# Revit family: BAS-IP_Видеодомофон_AU-04LA
name_source: partatom
category: Устройства связи
units: mm (PartAtom-declared; Revit-internal decimal feet)

## family parameters
Всегда вертикально = Да
На основе рабочей плоскости = Нет
Общий = Нет
При загрузке вырезать с полостями = Нет
Размер круглого соединителя = Использовать диаметр
Сохранять ориентацию аннотаций = Нет
Тип детали = Нормальный
Точка расчета площади = Нет

## types (2) — shared parameters
ADSK_Единица измерения = шт.
ADSK_Завод-изготовитель = BAS-IP
ADSK_Количество = 1
ADSK_Наименование = IP видеодомофон с экраном 4 дюйма
Встроенная камера = Нет
Габаритные размеры = 135 x 185 x 30 мм
Дисплей = 4,3” TFT LCD, сенсорный емкостный
Изготовитель = BAS-IP
Корпус = Пластик
Питание = PoE, +12 В
Потребление питания = 6 Вт, в режиме ожидания - 2,5 Вт
Разрешение экрана = 480 x 272
Тип установки = Настенный накладной

## per-type parameters (varying)
| type | ADSK_Марка | ADSK_Материал | Цве логотипа |
| Белый | AU-04LA White | White | Black |
| Черный | AU-04LA Black | Black | White |

note: column(s) folded — value = type name in every type: Цветовое решение
